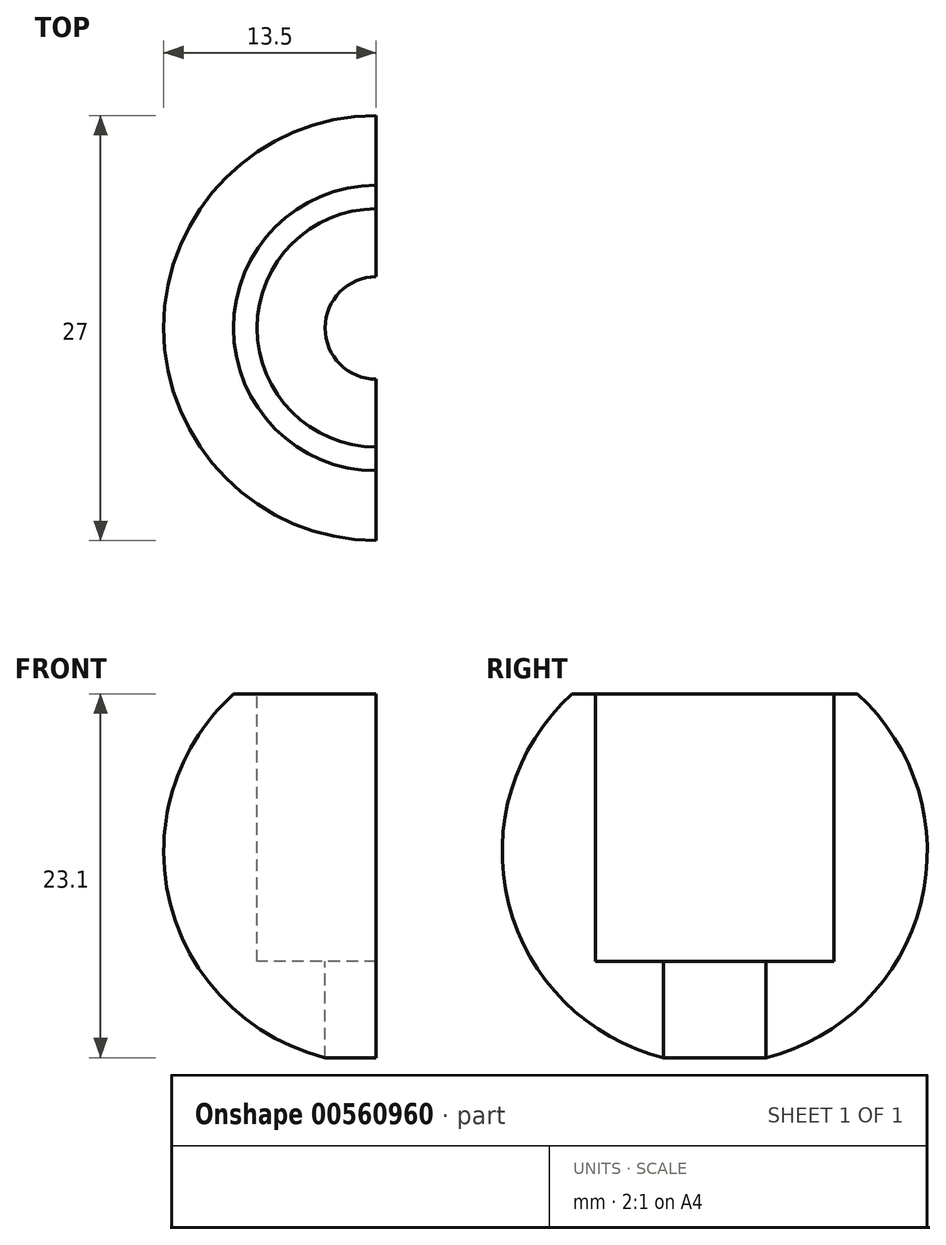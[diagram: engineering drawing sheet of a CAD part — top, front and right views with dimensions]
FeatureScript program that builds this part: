
annotation { "Feature Type Name" : "Feature", "Feature Type Description" : "" }
export const myFeature = defineFeature(function(context is Context, id is Id, definition is map)
    precondition{}
    {
        {
            var Q0;
            Q0=qCreatedBy(makeId("Front.planeOp"),FACE);
            var sketch = newSketch(context, id + "F0", { "sketchPlane" : qUnion([Q0])});
            skLineSegment(sketch, "E0", {"start": v(0, 0) * mm, "end": v(-13.5, 0) * mm});
            skLineSegment(sketch, "E1", {"start": v(0, 0) * mm, "end": v(0, 13.5) * mm});
            skArc(sketch, "E2", {"start": v(0, 13.5) * mm, "mid": v(-9.55, 9.55) * mm, "end": v(-13.5, 0) * mm});
            skSolve(sketch);
        }
        {
            var Q0;
            Q0=makeQuery(id+"F0.imprint","IMPRINT",FACE,{"disambiguationData":[TD([[makeQuery(id+"F0.imprint","IMPRINT",EDGE,{"derivedFrom":sQuery(id+"F0.wireOp",EDGE,"E0")}),-1.0]])]});
            var Q1;
            Q1=sQuery(id+"F0.wireOp",EDGE,"E0");
            revolve(context, id + "F1", {"entities" : qUnion([Q0]), "axis" : qUnion([Q1]), "revolveType" : RevolveType.FULL});
        }
        {
            var Q0;
            Q0=qCreatedBy(makeId("Top.planeOp"),FACE);
            var sketch = newSketch(context, id + "F2", { "sketchPlane" : qUnion([Q0])});
            skCircle(sketch, "E3", {"center": v(0, 0) * mm, "radius": 3.25 * mm});
            skSolve(sketch);
        }
        {
            var Q0;
            Q0 = qSketchRegion(id + "F2", true);
            extrude(context, id + "F3", {"entities" : qUnion([Q0]), "operationType" : NewBodyOperationType.REMOVE, "endBound" : BoundingType.THROUGH_ALL, "oppositeDirection" : true, "depth" : 25 * mm, "offsetDistance" : 25 * mm, "hasSecondDirection" : true, "secondDirectionBound" : BoundingType.THROUGH_ALL, "secondDirectionOppositeDirection" : false, "secondDirectionDepth" : 25 * mm});
        }
        {
            var Q0;
            Q0=qCreatedBy(makeId("Top.planeOp"),FACE);
            cPlane(context, id + "F4", {"entities" : qUnion([Q0]), "cplaneType" : CPlaneType.OFFSET, "offset" : 10 * mm, "width" : 150 * mm, "height" : 150 * mm});
        }
        {
            var Q0;
            Q0=qCreatedBy(id+"F4.planeOp",FACE);
            var sketch = newSketch(context, id + "F5", { "sketchPlane" : qUnion([Q0])});
            skCircle(sketch, "E4", {"center": v(0, 0) * mm, "radius": 13.5 * mm});
            skSolve(sketch);
        }
        {
            var Q0;
            Q0=makeQuery(id+"F5.imprint","IMPRINT",FACE,{"disambiguationData":[TD([[makeQuery(id+"F5.imprint","IMPRINT",EDGE,{"derivedFrom":sQuery(id+"F5.wireOp",EDGE,"E4")}),1.0]])]});
            extrude(context, id + "F6", {"entities" : qUnion([Q0]), "operationType" : NewBodyOperationType.REMOVE, "endBound" : BoundingType.THROUGH_ALL, "depth" : 25 * mm, "offsetDistance" : 25 * mm});
        }
        {
            var Q0;
            {var subQ0=makeQuery(id+"F1.opRevolve","SWEPT_FACE",FACE,{"disambiguationData":[OSD([sQuery(id+"F0.wireOp",EDGE,"E1")])]});Q0=makeQuery(id+"F6.boolean.opBoolean","COPY",FACE,{"disambiguationData":[TD([subQ0])],"derivedFrom":makeQuery(id+"F6.opExtrude","CAP_FACE",FACE,{"disambiguationData":[OSD([sQuery(id+"F5.wireOp",EDGE,"E4")])],"isStart":true})});}
            var sketch = newSketch(context, id + "F7", { "sketchPlane" : qUnion([Q0])});
            skCircle(sketch, "E5", {"center": v(0, 0) * mm, "radius": 7.57 * mm});
            skSolve(sketch);
        }
        {
            var Q0;
            {var subQ1=makeQuery(id+"F6.opExtrude","CAP_FACE",FACE,{"disambiguationData":[OSD([sQuery(id+"F5.wireOp",EDGE,"E4")])],"isStart":true});var subQ2=makeQuery(id+"F1.opRevolve","SWEPT_FACE",FACE,{"disambiguationData":[OSD([sQuery(id+"F0.wireOp",EDGE,"E1")])]});var subQ7=makeQuery(id+"F6.boolean.opBoolean","INTERSECT",EDGE,{"derivedFrom":[makeQuery(id+"F3.boolean.opBoolean","COPY",FACE,{"disambiguationData":[TD([subQ2])],"derivedFrom":makeQuery(id+"F3.opExtrude","SWEPT_FACE",FACE,{"disambiguationData":[OSD([sQuery(id+"F2.wireOp",EDGE,"E3")])]})}),subQ1]});Q0=makeQuery(id+"F7.imprint","IMPRINT",FACE,{"disambiguationData":[TD([[makeQuery(id+"F7.imprint","IMPRINT",EDGE,{"derivedFrom":subQ7}),1.0]])]});}
            var Q1;
            {var subQ1=makeQuery(id+"F6.opExtrude","CAP_FACE",FACE,{"disambiguationData":[OSD([sQuery(id+"F5.wireOp",EDGE,"E4")])],"isStart":true});var subQ2=makeQuery(id+"F1.opRevolve","SWEPT_FACE",FACE,{"disambiguationData":[OSD([sQuery(id+"F0.wireOp",EDGE,"E1")])]});var subQ7=makeQuery(id+"F6.boolean.opBoolean","INTERSECT",EDGE,{"derivedFrom":[makeQuery(id+"F3.boolean.opBoolean","COPY",FACE,{"disambiguationData":[TD([subQ2])],"derivedFrom":makeQuery(id+"F3.opExtrude","SWEPT_FACE",FACE,{"disambiguationData":[OSD([sQuery(id+"F2.wireOp",EDGE,"E3")])]})}),subQ1]});Q1=makeQuery(id+"F7.imprint","IMPRINT",FACE,{"disambiguationData":[TD([[makeQuery(id+"F7.imprint","IMPRINT",EDGE,{"derivedFrom":subQ7}),-1.0]])]});}
            extrude(context, id + "F8", {"entities" : qUnion([Q0, Q1]), "operationType" : NewBodyOperationType.REMOVE, "oppositeDirection" : true, "depth" : 17 * mm, "offsetDistance" : 25 * mm});
        }
    });
